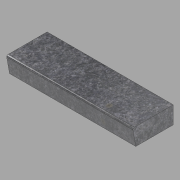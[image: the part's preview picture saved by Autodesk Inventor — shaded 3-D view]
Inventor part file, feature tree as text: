
AUTODESK INVENTOR PART (.ipt)
format: ipt  version: 2022.1 (Build 261234020, 234B)  size: 101,376 bytes
history: native  units: in
note: dims shown in document units (in); Inventor stores cm internally (conversion verified against a paired STEP export)
features: extrude x1, sketch x1
ambient origin geometry x8: Origin, YZ Plane, XZ Plane, XY Plane, X Axis, Y Axis, Z Axis, Center Point
bodies: Solid1 (feature_tree)
feature tree (2):
  extrude  "Extrusion1"  Depth=13.0in
  sketch  "Sketch1"  dims[d0=6.0in d1=13.0in d2=13.5in d3=0.5in d4=43.7083in d5=0.0in]
